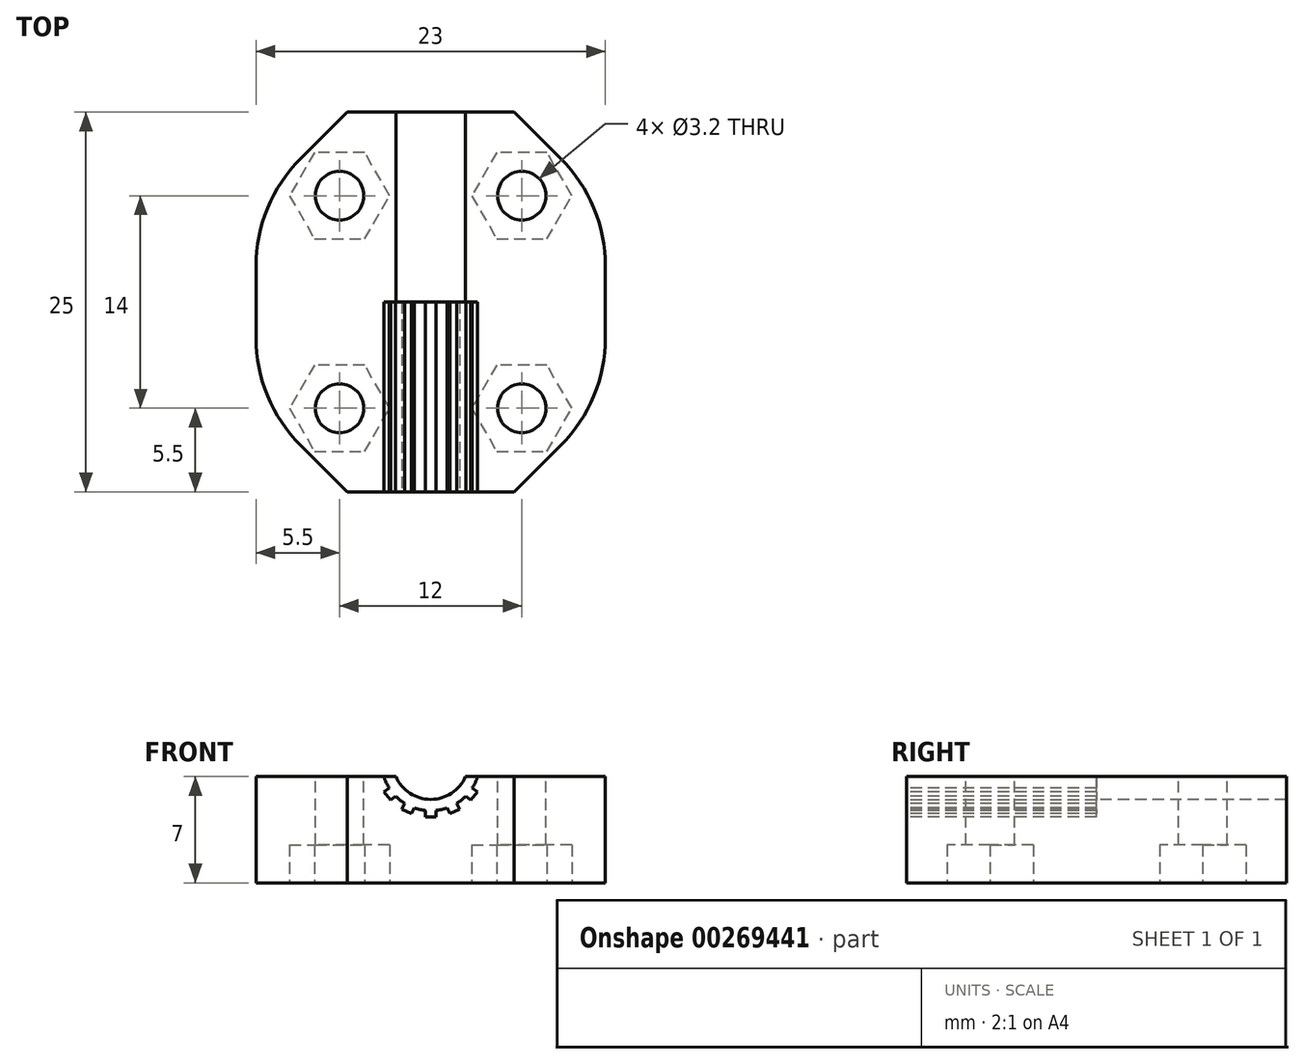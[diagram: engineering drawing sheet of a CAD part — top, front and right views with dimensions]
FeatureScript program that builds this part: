
annotation { "Feature Type Name" : "Feature", "Feature Type Description" : "" }
export const myFeature = defineFeature(function(context is Context, id is Id, definition is map)
    precondition{}
    {
        {
            var Q0;
            Q0=qCreatedBy(makeId("Top.planeOp"),FACE);
            var sketch = newSketch(context, id + "F0", { "sketchPlane" : qUnion([Q0])});
            skLineSegment(sketch, "E0.bottom", {"start": v(11.5, 12.5) * mm, "end": v(-11.5, 12.5) * mm});
            skLineSegment(sketch, "E0.top", {"start": v(11.5, -12.5) * mm, "end": v(-11.5, -12.5) * mm});
            skLineSegment(sketch, "E0.left", {"start": v(11.5, 12.5) * mm, "end": v(11.5, -12.5) * mm});
            skLineSegment(sketch, "E0.right", {"start": v(-11.5, 12.5) * mm, "end": v(-11.5, -12.5) * mm});
            skPoint(sketch, "E0.middle", {"position": v(0, 0) * mm});
            skLineSegment(sketch, "E1", {"start": v(11.5, -12.5) * mm, "end": v(-11.5, 12.5) * mm, "construction": true});
            skSolve(sketch);
        }
        {
            var Q0;
            Q0=qSketchRegion(id+"F0",true);
            extrude(context, id + "F1", {"entities" : qUnion([Q0]), "depth" : 7 * mm});
        }
        {
            var Q0;
            Q0=makeQuery(id+"F1.opExtrude","SWEPT_FACE",FACE,{"disambiguationData":[OSD([sQuery(id+"F0.wireOp",EDGE,"E0.top")])]});
            var sketch = newSketch(context, id + "F2", { "sketchPlane" : qUnion([Q0])});
            skCircle(sketch, "E2", {"center": v(0, 8) * mm, "radius": 2.5 * mm});
            skPoint(sketch, "E2.centerSnap0", {"position": v(0, 7) * mm});
            skLineSegment(sketch, "E3", {"start": v(0, 7) * mm, "end": v(0, 8) * mm});
            skCircle(sketch, "E4", {"center": v(0, 8) * mm, "radius": 3.25 * mm});
            skLineSegment(sketch, "E5", {"start": v(0, 7) * mm, "end": v(0, 5.02) * mm, "construction": true});
            skLineSegment(sketch, "E6.bottom", {"start": v(0.35, 4.35) * mm, "end": v(-0.35, 4.35) * mm});
            skLineSegment(sketch, "E6.top", {"start": v(0.35, 5.15) * mm, "end": v(-0.35, 5.15) * mm});
            skLineSegment(sketch, "E6.left", {"start": v(0.35, 4.35) * mm, "end": v(0.35, 5.15) * mm});
            skLineSegment(sketch, "E6.right", {"start": v(-0.35, 4.35) * mm, "end": v(-0.35, 5.15) * mm});
            skPoint(sketch, "E6.middle", {"position": v(0, 4.75) * mm});
            skLineSegment(sketch, "E7.1.0", {"start": v(-1.27, 4.56) * mm, "end": v(-0.92, 5.28) * mm});
            skLineSegment(sketch, "E7.1.1", {"start": v(-0.92, 5.28) * mm, "end": v(-1.55, 5.58) * mm});
            skLineSegment(sketch, "E7.1.2", {"start": v(-1.9, 4.86) * mm, "end": v(-1.55, 5.58) * mm});
            skLineSegment(sketch, "E7.1.3", {"start": v(-1.27, 4.56) * mm, "end": v(-1.9, 4.86) * mm});
            skLineSegment(sketch, "E7.2.0", {"start": v(-2.64, 5.45) * mm, "end": v(-2, 5.95) * mm});
            skLineSegment(sketch, "E7.2.1", {"start": v(-2, 5.95) * mm, "end": v(-2.45, 6.5) * mm});
            skLineSegment(sketch, "E7.2.2", {"start": v(-3.07, 6) * mm, "end": v(-2.45, 6.5) * mm});
            skLineSegment(sketch, "E7.2.3", {"start": v(-2.64, 5.45) * mm, "end": v(-3.07, 6) * mm});
            skLineSegment(sketch, "E7.3.0", {"start": v(-3.48, 6.85) * mm, "end": v(-2.7, 7.02) * mm});
            skLineSegment(sketch, "E7.3.1", {"start": v(-2.7, 7.02) * mm, "end": v(-2.86, 7.7) * mm});
            skLineSegment(sketch, "E7.3.2", {"start": v(-3.64, 7.53) * mm, "end": v(-2.86, 7.7) * mm});
            skLineSegment(sketch, "E7.3.3", {"start": v(-3.48, 6.85) * mm, "end": v(-3.64, 7.53) * mm});
            skLineSegment(sketch, "E7.4.0", {"start": v(-3.64, 8.47) * mm, "end": v(-2.86, 8.3) * mm});
            skLineSegment(sketch, "E7.4.1", {"start": v(-2.86, 8.3) * mm, "end": v(-2.7, 8.98) * mm});
            skLineSegment(sketch, "E7.4.2", {"start": v(-3.48, 9.15) * mm, "end": v(-2.7, 8.98) * mm});
            skLineSegment(sketch, "E7.4.3", {"start": v(-3.64, 8.47) * mm, "end": v(-3.48, 9.15) * mm});
            skLineSegment(sketch, "E7.5.0", {"start": v(-3.07, 10) * mm, "end": v(-2.45, 9.5) * mm});
            skLineSegment(sketch, "E7.5.1", {"start": v(-2.45, 9.5) * mm, "end": v(-2, 10.05) * mm});
            skLineSegment(sketch, "E7.5.2", {"start": v(-2.64, 10.55) * mm, "end": v(-2, 10.05) * mm});
            skLineSegment(sketch, "E7.5.3", {"start": v(-3.07, 10) * mm, "end": v(-2.64, 10.55) * mm});
            skLineSegment(sketch, "E7.6.0", {"start": v(-1.9, 11.14) * mm, "end": v(-1.55, 10.42) * mm});
            skLineSegment(sketch, "E7.6.1", {"start": v(-1.55, 10.42) * mm, "end": v(-0.92, 10.72) * mm});
            skLineSegment(sketch, "E7.6.2", {"start": v(-1.27, 11.44) * mm, "end": v(-0.92, 10.72) * mm});
            skLineSegment(sketch, "E7.6.3", {"start": v(-1.9, 11.14) * mm, "end": v(-1.27, 11.44) * mm});
            skLineSegment(sketch, "E7.7.0", {"start": v(-0.35, 11.65) * mm, "end": v(-0.35, 10.85) * mm});
            skLineSegment(sketch, "E7.7.1", {"start": v(-0.35, 10.85) * mm, "end": v(0.35, 10.85) * mm});
            skLineSegment(sketch, "E7.7.2", {"start": v(0.35, 11.65) * mm, "end": v(0.35, 10.85) * mm});
            skLineSegment(sketch, "E7.7.3", {"start": v(-0.35, 11.65) * mm, "end": v(0.35, 11.65) * mm});
            skLineSegment(sketch, "E7.8.0", {"start": v(1.27, 11.44) * mm, "end": v(0.92, 10.72) * mm});
            skLineSegment(sketch, "E7.8.1", {"start": v(0.92, 10.72) * mm, "end": v(1.55, 10.42) * mm});
            skLineSegment(sketch, "E7.8.2", {"start": v(1.9, 11.14) * mm, "end": v(1.55, 10.42) * mm});
            skLineSegment(sketch, "E7.8.3", {"start": v(1.27, 11.44) * mm, "end": v(1.9, 11.14) * mm});
            skLineSegment(sketch, "E7.9.0", {"start": v(2.64, 10.55) * mm, "end": v(2, 10.05) * mm});
            skLineSegment(sketch, "E7.9.1", {"start": v(2, 10.05) * mm, "end": v(2.45, 9.5) * mm});
            skLineSegment(sketch, "E7.9.2", {"start": v(3.07, 10) * mm, "end": v(2.45, 9.5) * mm});
            skLineSegment(sketch, "E7.9.3", {"start": v(2.64, 10.55) * mm, "end": v(3.07, 10) * mm});
            skLineSegment(sketch, "E7.10.0", {"start": v(3.48, 9.15) * mm, "end": v(2.7, 8.98) * mm});
            skLineSegment(sketch, "E7.10.1", {"start": v(2.7, 8.98) * mm, "end": v(2.86, 8.3) * mm});
            skLineSegment(sketch, "E7.10.2", {"start": v(3.64, 8.47) * mm, "end": v(2.86, 8.3) * mm});
            skLineSegment(sketch, "E7.10.3", {"start": v(3.48, 9.15) * mm, "end": v(3.64, 8.47) * mm});
            skLineSegment(sketch, "E7.11.0", {"start": v(3.64, 7.53) * mm, "end": v(2.86, 7.7) * mm});
            skLineSegment(sketch, "E7.11.1", {"start": v(2.86, 7.7) * mm, "end": v(2.7, 7.02) * mm});
            skLineSegment(sketch, "E7.11.2", {"start": v(3.48, 6.85) * mm, "end": v(2.7, 7.02) * mm});
            skLineSegment(sketch, "E7.11.3", {"start": v(3.64, 7.53) * mm, "end": v(3.48, 6.85) * mm});
            skLineSegment(sketch, "E7.12.0", {"start": v(3.07, 6) * mm, "end": v(2.45, 6.5) * mm});
            skLineSegment(sketch, "E7.12.1", {"start": v(2.45, 6.5) * mm, "end": v(2, 5.95) * mm});
            skLineSegment(sketch, "E7.12.2", {"start": v(2.64, 5.45) * mm, "end": v(2, 5.95) * mm});
            skLineSegment(sketch, "E7.12.3", {"start": v(3.07, 6) * mm, "end": v(2.64, 5.45) * mm});
            skLineSegment(sketch, "E7.13.0", {"start": v(1.9, 4.86) * mm, "end": v(1.55, 5.58) * mm});
            skLineSegment(sketch, "E7.13.1", {"start": v(1.55, 5.58) * mm, "end": v(0.92, 5.28) * mm});
            skLineSegment(sketch, "E7.13.2", {"start": v(1.27, 4.56) * mm, "end": v(0.92, 5.28) * mm});
            skLineSegment(sketch, "E7.13.3", {"start": v(1.9, 4.86) * mm, "end": v(1.27, 4.56) * mm});
            skLineSegment(sketch, "E7.anchor1", {"start": v(0, 8) * mm, "end": v(0.35, 5.15) * mm, "construction": true});
            skLineSegment(sketch, "E7.anchor2", {"start": v(0, 8) * mm, "end": v(0.35, 5.15) * mm, "construction": true});
            skSolve(sketch);
        }
        {
            var Q0;
            {var subQ1=makeQuery(id+"F1.opExtrude","CAP_EDGE",EDGE,{"disambiguationData":[OSD([sQuery(id+"F0.wireOp",EDGE,"E0.top")])],"isStart":false});var subQ4=makeQuery(id+"F2.imprint","IMPRINT",VERTEX,{"derivedFrom":subQ1});Q0=makeQuery(id+"F2.imprint","IMPRINT",FACE,{"disambiguationData":[TD([[makeQuery(id+"F2.imprint","IMPRINT",EDGE,{"disambiguationData":[TD([[subQ4,1.0]])],"derivedFrom":subQ1}),1.0]])]});}
            extrude(context, id + "F3", {"entities" : qUnion([Q0]), "operationType" : NewBodyOperationType.REMOVE, "endBound" : BoundingType.THROUGH_ALL, "oppositeDirection" : true, "depth" : 25 * mm});
        }
        {
            var Q0;
            {var subQ0=sQuery(id+"F2.wireOp",EDGE,"E2");var subQ1=makeQuery(id+"F1.opExtrude","CAP_EDGE",EDGE,{"disambiguationData":[OSD([sQuery(id+"F0.wireOp",EDGE,"E0.top")])],"isStart":false});var subQ2=makeQuery(id+"F2.imprint","INTERSECT",VERTEX,{"disambiguationData":[OD(0.0)],"derivedFrom":[subQ1,subQ0]});Q0=makeQuery(id+"F2.imprint","IMPRINT",FACE,{"disambiguationData":[TD([[makeQuery(id+"F2.imprint","IMPRINT",EDGE,{"disambiguationData":[TD([[subQ2,-1.0]])],"derivedFrom":subQ0}),-1.0]])]});}
            var Q1;
            Q1=makeQuery(id+"F2.imprint","IMPRINT",FACE,{"disambiguationData":[TD([[makeQuery(id+"F2.imprint","IMPRINT",EDGE,{"derivedFrom":sQuery(id+"F2.wireOp",EDGE,"E7.12.0")}),1.0]])]});
            var Q2;
            Q2=makeQuery(id+"F2.imprint","IMPRINT",FACE,{"disambiguationData":[TD([[makeQuery(id+"F2.imprint","IMPRINT",EDGE,{"derivedFrom":sQuery(id+"F2.wireOp",EDGE,"E7.13.0")}),1.0]])]});
            var Q3;
            Q3=makeQuery(id+"F2.imprint","IMPRINT",FACE,{"disambiguationData":[TD([[makeQuery(id+"F2.imprint","IMPRINT",EDGE,{"derivedFrom":sQuery(id+"F2.wireOp",EDGE,"E6.left")}),1.0]])]});
            var Q4;
            Q4=makeQuery(id+"F2.imprint","IMPRINT",FACE,{"disambiguationData":[TD([[makeQuery(id+"F2.imprint","IMPRINT",EDGE,{"derivedFrom":sQuery(id+"F2.wireOp",EDGE,"E7.1.0")}),1.0]])]});
            var Q5;
            Q5=makeQuery(id+"F2.imprint","IMPRINT",FACE,{"disambiguationData":[TD([[makeQuery(id+"F2.imprint","IMPRINT",EDGE,{"derivedFrom":sQuery(id+"F2.wireOp",EDGE,"E7.2.0")}),1.0]])]});
            var Q6;
            {var subQ0=sQuery(id+"F2.wireOp",EDGE,"E7.11.2");var subQ1=sQuery(id+"F2.wireOp",EDGE,"E4");var subQ2=makeQuery(id+"F2.imprint","INTERSECT",VERTEX,{"derivedFrom":[subQ1,subQ0]});Q6=makeQuery(id+"F2.imprint","IMPRINT",FACE,{"disambiguationData":[TD([[makeQuery(id+"F2.imprint","IMPRINT",EDGE,{"disambiguationData":[TD([[subQ2,-1.0]])],"derivedFrom":subQ1}),1.0]])]});}
            var Q7;
            {var subQ0=sQuery(id+"F2.wireOp",EDGE,"E7.3.0");var subQ1=sQuery(id+"F2.wireOp",EDGE,"E4");var subQ2=makeQuery(id+"F2.imprint","INTERSECT",VERTEX,{"derivedFrom":[subQ1,subQ0]});Q7=makeQuery(id+"F2.imprint","IMPRINT",FACE,{"disambiguationData":[TD([[makeQuery(id+"F2.imprint","IMPRINT",EDGE,{"disambiguationData":[TD([[subQ2,1.0]])],"derivedFrom":subQ1}),1.0]])]});}
            extrude(context, id + "F4", {"entities" : qUnion([Q0, Q1, Q2, Q3, Q4, Q5, Q6, Q7]), "operationType" : NewBodyOperationType.REMOVE, "oppositeDirection" : true, "depth" : 12.5 * mm});
        }
        {
            var Q0;
            Q0=makeQuery(id+"F1.opExtrude","SWEPT_EDGE",EDGE,{"disambiguationData":[OSD([sQuery(id+"F0.wireOp",EDGE,"E0.top"),sQuery(id+"F0.wireOp",EDGE,"E0.left")])]});
            var Q1;
            Q1=makeQuery(id+"F1.opExtrude","SWEPT_EDGE",EDGE,{"disambiguationData":[OSD([sQuery(id+"F0.wireOp",EDGE,"E0.top"),sQuery(id+"F0.wireOp",EDGE,"E0.right")])]});
            var Q2;
            Q2=makeQuery(id+"F1.opExtrude","SWEPT_EDGE",EDGE,{"disambiguationData":[OSD([sQuery(id+"F0.wireOp",EDGE,"E0.bottom"),sQuery(id+"F0.wireOp",EDGE,"E0.left")])]});
            var Q3;
            Q3=makeQuery(id+"F1.opExtrude","SWEPT_EDGE",EDGE,{"disambiguationData":[OSD([sQuery(id+"F0.wireOp",EDGE,"E0.bottom"),sQuery(id+"F0.wireOp",EDGE,"E0.right")])]});
            chamfer(context, id + "F5", {"entities" : qUnion([Q0, Q1, Q2, Q3]), "width" : 6 * mm, "tangentPropagation" : true});
        }
        {
            var Q0;
            {var subQ0=sQuery(id+"F0.wireOp",EDGE,"E0.left");Q0=makeQuery(id+"F5.opChamfer","BLEND_EDGE",EDGE,{"blendedFrom":[makeQuery(id+"F1.opExtrude","SWEPT_EDGE",EDGE,{"disambiguationData":[OSD([sQuery(id+"F0.wireOp",EDGE,"E0.bottom"),subQ0])]}),makeQuery(id+"F1.opExtrude","SWEPT_FACE",FACE,{"disambiguationData":[OSD([subQ0])]})],"blendedInto":[makeQuery(id+"F1.opExtrude","SWEPT_FACE",FACE,{"disambiguationData":[OSD([subQ0])]})]});}
            var Q1;
            {var subQ0=sQuery(id+"F0.wireOp",EDGE,"E0.left");Q1=makeQuery(id+"F5.opChamfer","BLEND_EDGE",EDGE,{"blendedFrom":[makeQuery(id+"F1.opExtrude","SWEPT_EDGE",EDGE,{"disambiguationData":[OSD([sQuery(id+"F0.wireOp",EDGE,"E0.top"),subQ0])]}),makeQuery(id+"F1.opExtrude","SWEPT_FACE",FACE,{"disambiguationData":[OSD([subQ0])]})],"blendedInto":[makeQuery(id+"F1.opExtrude","SWEPT_FACE",FACE,{"disambiguationData":[OSD([subQ0])]})]});}
            var Q2;
            {var subQ0=sQuery(id+"F0.wireOp",EDGE,"E0.right");Q2=makeQuery(id+"F5.opChamfer","BLEND_EDGE",EDGE,{"blendedFrom":[makeQuery(id+"F1.opExtrude","SWEPT_EDGE",EDGE,{"disambiguationData":[OSD([sQuery(id+"F0.wireOp",EDGE,"E0.bottom"),subQ0])]}),makeQuery(id+"F1.opExtrude","SWEPT_FACE",FACE,{"disambiguationData":[OSD([subQ0])]})],"blendedInto":[makeQuery(id+"F1.opExtrude","SWEPT_FACE",FACE,{"disambiguationData":[OSD([subQ0])]})]});}
            var Q3;
            {var subQ0=sQuery(id+"F0.wireOp",EDGE,"E0.right");Q3=makeQuery(id+"F5.opChamfer","BLEND_EDGE",EDGE,{"blendedFrom":[makeQuery(id+"F1.opExtrude","SWEPT_EDGE",EDGE,{"disambiguationData":[OSD([sQuery(id+"F0.wireOp",EDGE,"E0.top"),subQ0])]}),makeQuery(id+"F1.opExtrude","SWEPT_FACE",FACE,{"disambiguationData":[OSD([subQ0])]})],"blendedInto":[makeQuery(id+"F1.opExtrude","SWEPT_FACE",FACE,{"disambiguationData":[OSD([subQ0])]})]});}
            fillet(context, id + "F6", {"entities" : qUnion([Q0, Q1, Q2, Q3]), "radius" : 10 * mm, "tangentPropagation" : true, "allowEdgeOverflow" : false});
        }
        {
            var Q0;
            {var subQ0=sQuery(id+"F0.wireOp",EDGE,"E0.bottom");var subQ1=sQuery(id+"F0.wireOp",EDGE,"E0.top");var subQ2=sQuery(id+"F0.wireOp",EDGE,"E0.left");Q0=makeQuery(id+"F3.boolean.opBoolean","SPLIT",FACE,{"disambiguationData":[TD([makeQuery(id+"F1.opExtrude","SWEPT_FACE",FACE,{"disambiguationData":[OSD([subQ2])]})])],"derivedFrom":makeQuery(id+"F1.opExtrude","CAP_FACE",FACE,{"disambiguationData":[OSD([subQ0,subQ1,subQ2,sQuery(id+"F0.wireOp",EDGE,"E0.right")])],"isStart":false})});}
            var sketch = newSketch(context, id + "F7", { "sketchPlane" : qUnion([Q0])});
            skLineSegment(sketch, "E8.bottom", {"start": v(-6, -7) * mm, "end": v(6, -7) * mm, "construction": true});
            skLineSegment(sketch, "E8.top", {"start": v(-6, 7) * mm, "end": v(6, 7) * mm, "construction": true});
            skLineSegment(sketch, "E8.left", {"start": v(-6, -7) * mm, "end": v(-6, 7) * mm, "construction": true});
            skLineSegment(sketch, "E8.right", {"start": v(6, -7) * mm, "end": v(6, 7) * mm, "construction": true});
            skPoint(sketch, "E8.middle", {"position": v(0, 0) * mm});
            skCircle(sketch, "E9", {"center": v(6, -7) * mm, "radius": 1.6 * mm});
            skCircle(sketch, "E10", {"center": v(-6, -7) * mm, "radius": 1.6 * mm});
            skCircle(sketch, "E11", {"center": v(-6, 7) * mm, "radius": 1.6 * mm});
            skCircle(sketch, "E12", {"center": v(6, 7) * mm, "radius": 1.6 * mm});
            skSolve(sketch);
        }
        {
            var Q0;
            Q0=qSketchRegion(id+"F7",true);
            extrude(context, id + "F8", {"entities" : qUnion([Q0]), "operationType" : NewBodyOperationType.REMOVE, "oppositeDirection" : true, "depth" : 25 * mm});
        }
        {
            var Q0;
            Q0=makeQuery(id+"F1.opExtrude","CAP_FACE",FACE,{"disambiguationData":[OSD([sQuery(id+"F0.wireOp",EDGE,"E0.bottom"),sQuery(id+"F0.wireOp",EDGE,"E0.top"),sQuery(id+"F0.wireOp",EDGE,"E0.left"),sQuery(id+"F0.wireOp",EDGE,"E0.right")])],"isStart":true});
            var sketch = newSketch(context, id + "F9", { "sketchPlane" : qUnion([Q0])});
            skCircle(sketch, "E13.cCircle", {"center": v(-6, 7) * mm, "radius": 2.85 * mm, "construction": true});
            skLineSegment(sketch, "E13.0", {"start": v(-2.7, 7) * mm, "end": v(-4.35, 4.15) * mm});
            skLineSegment(sketch, "E13.1", {"start": v(-4.35, 4.15) * mm, "end": v(-7.65, 4.15) * mm});
            skLineSegment(sketch, "E13.2", {"start": v(-7.65, 4.15) * mm, "end": v(-9.3, 7) * mm});
            skLineSegment(sketch, "E13.3", {"start": v(-9.3, 7) * mm, "end": v(-7.65, 9.85) * mm});
            skLineSegment(sketch, "E13.4", {"start": v(-7.65, 9.85) * mm, "end": v(-4.35, 9.85) * mm});
            skLineSegment(sketch, "E13.5", {"start": v(-4.35, 9.85) * mm, "end": v(-2.7, 7) * mm});
            skPoint(sketch, "E13.0.midPoint", {"position": v(-3.53, 5.57) * mm});
            skLineSegment(sketch, "E14.0.1.0", {"start": v(-7.65, -9.85) * mm, "end": v(-9.3, -7) * mm});
            skLineSegment(sketch, "E14.0.1.1", {"start": v(-7.65, -4.15) * mm, "end": v(-4.35, -4.15) * mm});
            skLineSegment(sketch, "E14.0.1.2", {"start": v(-9.3, -7) * mm, "end": v(-7.65, -4.15) * mm});
            skPoint(sketch, "E14.0.1.3", {"position": v(-3.53, -8.43) * mm});
            skLineSegment(sketch, "E14.0.1.4", {"start": v(-4.35, -4.15) * mm, "end": v(-2.7, -7) * mm});
            skLineSegment(sketch, "E14.0.1.5", {"start": v(-4.35, -9.85) * mm, "end": v(-7.65, -9.85) * mm});
            skLineSegment(sketch, "E14.0.1.6", {"start": v(-2.7, -7) * mm, "end": v(-4.35, -9.85) * mm});
            skCircle(sketch, "E14.0.1.7", {"center": v(-6, -7) * mm, "radius": 2.85 * mm, "construction": true});
            skLineSegment(sketch, "E14.1.0.0", {"start": v(4.35, 4.15) * mm, "end": v(2.7, 7) * mm});
            skLineSegment(sketch, "E14.1.0.1", {"start": v(4.35, 9.85) * mm, "end": v(7.65, 9.85) * mm});
            skLineSegment(sketch, "E14.1.0.2", {"start": v(2.7, 7) * mm, "end": v(4.35, 9.85) * mm});
            skPoint(sketch, "E14.1.0.3", {"position": v(8.47, 5.57) * mm});
            skLineSegment(sketch, "E14.1.0.4", {"start": v(7.65, 9.85) * mm, "end": v(9.3, 7) * mm});
            skLineSegment(sketch, "E14.1.0.5", {"start": v(7.65, 4.15) * mm, "end": v(4.35, 4.15) * mm});
            skLineSegment(sketch, "E14.1.0.6", {"start": v(9.3, 7) * mm, "end": v(7.65, 4.15) * mm});
            skCircle(sketch, "E14.1.0.7", {"center": v(6, 7) * mm, "radius": 2.85 * mm, "construction": true});
            skLineSegment(sketch, "E14.1.1.0", {"start": v(4.35, -9.85) * mm, "end": v(2.7, -7) * mm});
            skLineSegment(sketch, "E14.1.1.1", {"start": v(4.35, -4.15) * mm, "end": v(7.65, -4.15) * mm});
            skLineSegment(sketch, "E14.1.1.2", {"start": v(2.7, -7) * mm, "end": v(4.35, -4.15) * mm});
            skPoint(sketch, "E14.1.1.3", {"position": v(8.47, -8.43) * mm});
            skLineSegment(sketch, "E14.1.1.4", {"start": v(7.65, -4.15) * mm, "end": v(9.3, -7) * mm});
            skLineSegment(sketch, "E14.1.1.5", {"start": v(7.65, -9.85) * mm, "end": v(4.35, -9.85) * mm});
            skLineSegment(sketch, "E14.1.1.6", {"start": v(9.3, -7) * mm, "end": v(7.65, -9.85) * mm});
            skCircle(sketch, "E14.1.1.7", {"center": v(6, -7) * mm, "radius": 2.85 * mm, "construction": true});
            skLineSegment(sketch, "E14.direction1", {"start": v(-7.65, 4.15) * mm, "end": v(4.35, 4.15) * mm, "construction": true});
            skLineSegment(sketch, "E14.direction2", {"start": v(-7.65, 4.15) * mm, "end": v(-7.65, -9.85) * mm, "construction": true});
            skSolve(sketch);
        }
        {
            var Q0;
            Q0 = qSketchRegion(id + "F9", true);
            extrude(context, id + "F10", {"entities" : qUnion([Q0]), "operationType" : NewBodyOperationType.REMOVE, "oppositeDirection" : true, "depth" : 2.5 * mm});
        }
    });
